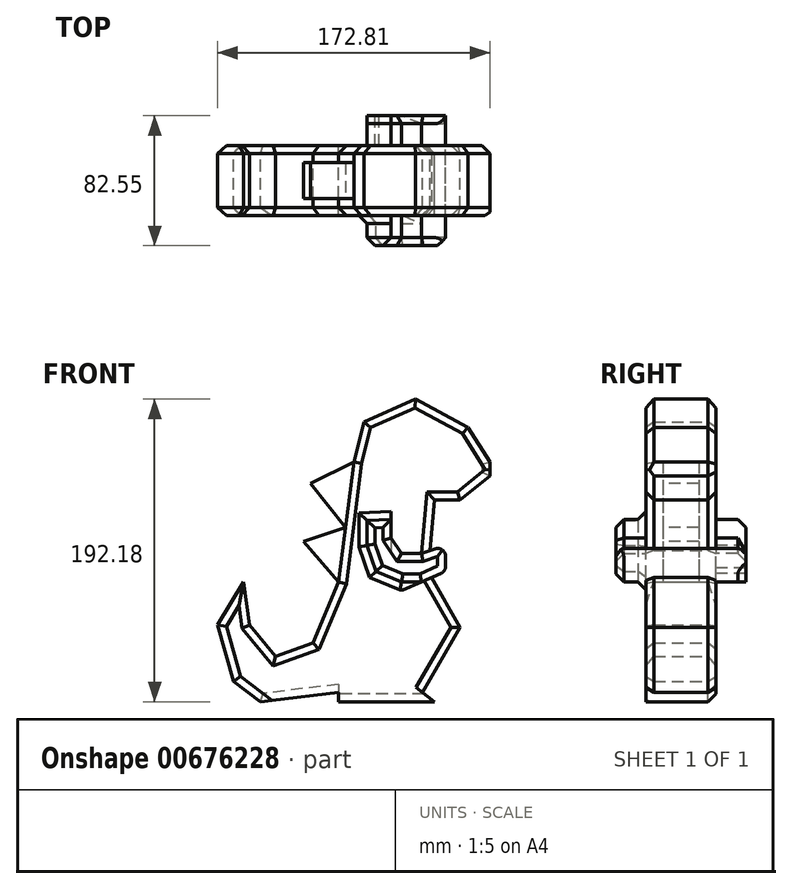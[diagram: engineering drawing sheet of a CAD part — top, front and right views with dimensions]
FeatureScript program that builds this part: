
annotation { "Feature Type Name" : "Feature", "Feature Type Description" : "" }
export const myFeature = defineFeature(function(context is Context, id is Id, definition is map)
    precondition{}
    {
        {
            var Q0;
            Q0=qCreatedBy(makeId("Front.planeOp"),FACE);
            var sketch = newSketch(context, id + "F0", { "sketchPlane" : qUnion([Q0])});
            skLineSegment(sketch, "E0", {"start": v(77.08, 51.94) * mm, "end": v(77.08, 55.91) * mm});
            skLineSegment(sketch, "E1", {"start": v(-60.47, 0) * mm, "end": v(-76.86, -27.51) * mm});
            skLineSegment(sketch, "E2", {"start": v(-76.86, -27.51) * mm, "end": v(-66.68, -63.13) * mm});
            skLineSegment(sketch, "E3", {"start": v(-60.47, 0) * mm, "end": v(-56.5, -27.51) * mm});
            skLineSegment(sketch, "E4", {"start": v(-56.5, -27.51) * mm, "end": v(-40.11, -47.38) * mm});
            skLineSegment(sketch, "E5", {"start": v(-40.11, -47.38) * mm, "end": v(-16.28, -38.93) * mm});
            skLineSegment(sketch, "E6", {"start": v(-16.28, -38.93) * mm, "end": v(0, 0) * mm});
            skPoint(sketch, "E7.start.orphan", {"position": v(68.14, 60.88) * mm});
            skPoint(sketch, "E8.end.orphan", {"position": v(45.3, 0) * mm});
            skPoint(sketch, "E8.start.orphan", {"position": v(68.14, 10.23) * mm});
            skPoint(sketch, "E9.end.orphan", {"position": v(38.54, 76.27) * mm});
            skLineSegment(sketch, "E10", {"start": v(0, 0) * mm, "end": v(9.55, 76.27) * mm});
            skLineSegment(sketch, "E11", {"start": v(-49.55, -76.18) * mm, "end": v(-66.68, -63.13) * mm});
            skLineSegment(sketch, "E12", {"start": v(-49.55, -76.18) * mm, "end": v(0, -70.22) * mm});
            skLineSegment(sketch, "E13", {"start": v(0, -70.22) * mm, "end": v(0, -76.18) * mm});
            skLineSegment(sketch, "E14", {"start": v(0, -76.18) * mm, "end": v(60.7, -76.18) * mm});
            skLineSegment(sketch, "E15", {"start": v(60.7, -76.18) * mm, "end": v(53.24, -70.22) * mm});
            skLineSegment(sketch, "E16", {"start": v(53.24, -70.22) * mm, "end": v(77.08, -29) * mm});
            skLineSegment(sketch, "E17", {"start": v(77.08, -29) * mm, "end": v(56.72, 6.75) * mm});
            skLineSegment(sketch, "E18", {"start": v(56.72, 6.75) * mm, "end": v(60.7, 51.94) * mm});
            skLineSegment(sketch, "E19", {"start": v(60.7, 51.94) * mm, "end": v(77.08, 51.94) * mm});
            skPoint(sketch, "E19.endSnap0", {"position": v(77.08, 55.91) * mm});
            skLineSegment(sketch, "E20", {"start": v(77.08, 51.94) * mm, "end": v(95.95, 67.33) * mm});
            skLineSegment(sketch, "E21", {"start": v(95.95, 67.33) * mm, "end": v(95.95, 76.27) * mm});
            skLineSegment(sketch, "E22", {"start": v(95.95, 76.27) * mm, "end": v(82.05, 98.12) * mm});
            skLineSegment(sketch, "E23", {"start": v(82.05, 98.12) * mm, "end": v(48.78, 116) * mm});
            skLineSegment(sketch, "E24", {"start": v(48.78, 116) * mm, "end": v(16, 101.6) * mm});
            skLineSegment(sketch, "E25", {"start": v(16, 101.6) * mm, "end": v(9.55, 76.27) * mm});
            skPoint(sketch, "E26.orphan", {"position": v(77.08, 76.27) * mm});
            skPoint(sketch, "E27.orphan", {"position": v(77.08, 35.55) * mm});
            skPoint(sketch, "E28.end.orphan", {"position": v(0, 76.27) * mm});
            skSolve(sketch);
        }
        {
            var Q0;
            Q0=makeQuery(id+"F0.imprint","IMPRINT",FACE,{"disambiguationData":[TD([[makeQuery(id+"F0.imprint","IMPRINT",EDGE,{"derivedFrom":sQuery(id+"F0.wireOp",EDGE,"E1")}),1.0]])]});
            extrude(context, id + "F1", {"entities" : qUnion([Q0]), "depth" : 44.45 * mm, "offsetDistance" : 25.4 * mm});
        }
        {
            var Q0;
            Q0=makeQuery(id+"F1.opExtrude","CAP_EDGE",EDGE,{"disambiguationData":[OSD([sQuery(id+"F0.wireOp",EDGE,"E24")])],"isStart":false});
            var Q1;
            Q1=makeQuery(id+"F1.opExtrude","CAP_EDGE",EDGE,{"disambiguationData":[OSD([sQuery(id+"F0.wireOp",EDGE,"E23")])],"isStart":false});
            var Q2;
            Q2=makeQuery(id+"F1.opExtrude","CAP_EDGE",EDGE,{"disambiguationData":[OSD([sQuery(id+"F0.wireOp",EDGE,"E22")])],"isStart":false});
            var Q3;
            Q3=makeQuery(id+"F1.opExtrude","CAP_EDGE",EDGE,{"disambiguationData":[OSD([sQuery(id+"F0.wireOp",EDGE,"E20")])],"isStart":false});
            var Q4;
            Q4=makeQuery(id+"F1.opExtrude","CAP_EDGE",EDGE,{"disambiguationData":[OSD([sQuery(id+"F0.wireOp",EDGE,"E19")])],"isStart":false});
            var Q5;
            Q5=makeQuery(id+"F1.opExtrude","CAP_EDGE",EDGE,{"disambiguationData":[OSD([sQuery(id+"F0.wireOp",EDGE,"E18")])],"isStart":false});
            var Q6;
            Q6=makeQuery(id+"F1.opExtrude","CAP_EDGE",EDGE,{"disambiguationData":[OSD([sQuery(id+"F0.wireOp",EDGE,"E17")])],"isStart":false});
            var Q7;
            Q7=makeQuery(id+"F1.opExtrude","CAP_EDGE",EDGE,{"disambiguationData":[OSD([sQuery(id+"F0.wireOp",EDGE,"E16")])],"isStart":false});
            var Q8;
            Q8=makeQuery(id+"F1.opExtrude","CAP_EDGE",EDGE,{"disambiguationData":[OSD([sQuery(id+"F0.wireOp",EDGE,"E10")])],"isStart":false});
            var Q9;
            Q9=makeQuery(id+"F1.opExtrude","CAP_EDGE",EDGE,{"disambiguationData":[OSD([sQuery(id+"F0.wireOp",EDGE,"E6")])],"isStart":false});
            var Q10;
            Q10=makeQuery(id+"F1.opExtrude","CAP_EDGE",EDGE,{"disambiguationData":[OSD([sQuery(id+"F0.wireOp",EDGE,"E25")])],"isStart":false});
            var Q11;
            Q11=makeQuery(id+"F1.opExtrude","CAP_EDGE",EDGE,{"disambiguationData":[OSD([sQuery(id+"F0.wireOp",EDGE,"E5")])],"isStart":false});
            var Q12;
            Q12=makeQuery(id+"F1.opExtrude","CAP_EDGE",EDGE,{"disambiguationData":[OSD([sQuery(id+"F0.wireOp",EDGE,"E4")])],"isStart":false});
            var Q13;
            Q13=makeQuery(id+"F1.opExtrude","CAP_EDGE",EDGE,{"disambiguationData":[OSD([sQuery(id+"F0.wireOp",EDGE,"E3")])],"isStart":false});
            var Q14;
            Q14=makeQuery(id+"F1.opExtrude","CAP_EDGE",EDGE,{"disambiguationData":[OSD([sQuery(id+"F0.wireOp",EDGE,"E1")])],"isStart":false});
            var Q15;
            Q15=makeQuery(id+"F1.opExtrude","CAP_EDGE",EDGE,{"disambiguationData":[OSD([sQuery(id+"F0.wireOp",EDGE,"E2")])],"isStart":false});
            var Q16;
            Q16=makeQuery(id+"F1.opExtrude","CAP_EDGE",EDGE,{"disambiguationData":[OSD([sQuery(id+"F0.wireOp",EDGE,"E11")])],"isStart":false});
            var Q17;
            Q17=makeQuery(id+"F1.opExtrude","CAP_EDGE",EDGE,{"disambiguationData":[OSD([sQuery(id+"F0.wireOp",EDGE,"E24")])],"isStart":true});
            var Q18;
            Q18=makeQuery(id+"F1.opExtrude","CAP_EDGE",EDGE,{"disambiguationData":[OSD([sQuery(id+"F0.wireOp",EDGE,"E23")])],"isStart":true});
            var Q19;
            Q19=makeQuery(id+"F1.opExtrude","CAP_EDGE",EDGE,{"disambiguationData":[OSD([sQuery(id+"F0.wireOp",EDGE,"E22")])],"isStart":true});
            var Q20;
            Q20=makeQuery(id+"F1.opExtrude","CAP_EDGE",EDGE,{"disambiguationData":[OSD([sQuery(id+"F0.wireOp",EDGE,"E21")])],"isStart":true});
            var Q21;
            Q21=makeQuery(id+"F1.opExtrude","CAP_EDGE",EDGE,{"disambiguationData":[OSD([sQuery(id+"F0.wireOp",EDGE,"E20")])],"isStart":true});
            var Q22;
            Q22=makeQuery(id+"F1.opExtrude","CAP_EDGE",EDGE,{"disambiguationData":[OSD([sQuery(id+"F0.wireOp",EDGE,"E19")])],"isStart":true});
            var Q23;
            Q23=makeQuery(id+"F1.opExtrude","CAP_EDGE",EDGE,{"disambiguationData":[OSD([sQuery(id+"F0.wireOp",EDGE,"E18")])],"isStart":true});
            var Q24;
            Q24=makeQuery(id+"F1.opExtrude","CAP_EDGE",EDGE,{"disambiguationData":[OSD([sQuery(id+"F0.wireOp",EDGE,"E17")])],"isStart":true});
            var Q25;
            Q25=makeQuery(id+"F1.opExtrude","CAP_EDGE",EDGE,{"disambiguationData":[OSD([sQuery(id+"F0.wireOp",EDGE,"E16")])],"isStart":true});
            var Q26;
            Q26=makeQuery(id+"F1.opExtrude","CAP_EDGE",EDGE,{"disambiguationData":[OSD([sQuery(id+"F0.wireOp",EDGE,"E14")])],"isStart":true});
            var Q27;
            Q27=makeQuery(id+"F1.opExtrude","CAP_EDGE",EDGE,{"disambiguationData":[OSD([sQuery(id+"F0.wireOp",EDGE,"E25")])],"isStart":true});
            var Q28;
            Q28=makeQuery(id+"F1.opExtrude","CAP_EDGE",EDGE,{"disambiguationData":[OSD([sQuery(id+"F0.wireOp",EDGE,"E10")])],"isStart":true});
            var Q29;
            Q29=makeQuery(id+"F1.opExtrude","CAP_EDGE",EDGE,{"disambiguationData":[OSD([sQuery(id+"F0.wireOp",EDGE,"E6")])],"isStart":true});
            var Q30;
            Q30=makeQuery(id+"F1.opExtrude","CAP_EDGE",EDGE,{"disambiguationData":[OSD([sQuery(id+"F0.wireOp",EDGE,"E5")])],"isStart":true});
            var Q31;
            Q31=makeQuery(id+"F1.opExtrude","CAP_EDGE",EDGE,{"disambiguationData":[OSD([sQuery(id+"F0.wireOp",EDGE,"E4")])],"isStart":true});
            var Q32;
            Q32=makeQuery(id+"F1.opExtrude","CAP_EDGE",EDGE,{"disambiguationData":[OSD([sQuery(id+"F0.wireOp",EDGE,"E3")])],"isStart":true});
            var Q33;
            Q33=makeQuery(id+"F1.opExtrude","CAP_EDGE",EDGE,{"disambiguationData":[OSD([sQuery(id+"F0.wireOp",EDGE,"E1")])],"isStart":true});
            var Q34;
            Q34=makeQuery(id+"F1.opExtrude","CAP_EDGE",EDGE,{"disambiguationData":[OSD([sQuery(id+"F0.wireOp",EDGE,"E2")])],"isStart":true});
            var Q35;
            Q35=makeQuery(id+"F1.opExtrude","CAP_EDGE",EDGE,{"disambiguationData":[OSD([sQuery(id+"F0.wireOp",EDGE,"E11")])],"isStart":true});
            var Q36;
            Q36=makeQuery(id+"F1.opExtrude","CAP_EDGE",EDGE,{"disambiguationData":[OSD([sQuery(id+"F0.wireOp",EDGE,"E12")])],"isStart":true});
            chamfer(context, id + "F2", {"entities" : qUnion([Q0, Q1, Q2, Q3, Q4, Q5, Q6, Q7, Q8, Q9, Q10, Q11, Q12, Q13, Q14, Q15, Q16, Q17, Q18, Q19, Q20, Q21, Q22, Q23, Q24, Q25, Q26, Q27, Q28, Q29, Q30, Q31, Q32, Q33, Q34, Q35, Q36]), "width" : 5.08 * mm, "tangentPropagation" : true});
        }
        {
            var Q0;
            Q0=makeQuery(id+"F1.opExtrude","CAP_FACE",FACE,{"disambiguationData":[OSD([sQuery(id+"F0.wireOp",EDGE,"E1"),sQuery(id+"F0.wireOp",EDGE,"E2"),sQuery(id+"F0.wireOp",EDGE,"E3"),sQuery(id+"F0.wireOp",EDGE,"E4"),sQuery(id+"F0.wireOp",EDGE,"E5"),sQuery(id+"F0.wireOp",EDGE,"E6"),sQuery(id+"F0.wireOp",EDGE,"E10"),sQuery(id+"F0.wireOp",EDGE,"E11"),sQuery(id+"F0.wireOp",EDGE,"E12"),sQuery(id+"F0.wireOp",EDGE,"E13"),sQuery(id+"F0.wireOp",EDGE,"E14"),sQuery(id+"F0.wireOp",EDGE,"E15"),sQuery(id+"F0.wireOp",EDGE,"E16"),sQuery(id+"F0.wireOp",EDGE,"E17"),sQuery(id+"F0.wireOp",EDGE,"E18"),sQuery(id+"F0.wireOp",EDGE,"E19"),sQuery(id+"F0.wireOp",EDGE,"E20"),sQuery(id+"F0.wireOp",EDGE,"E21"),sQuery(id+"F0.wireOp",EDGE,"E22"),sQuery(id+"F0.wireOp",EDGE,"E23"),sQuery(id+"F0.wireOp",EDGE,"E24"),sQuery(id+"F0.wireOp",EDGE,"E25")])],"isStart":true});
            var sketch = newSketch(context, id + "F3", { "sketchPlane" : qUnion([Q0])});
            skLineSegment(sketch, "E29", {"start": v(-33.23, 39.73) * mm, "end": v(-33.23, 27.8) * mm});
            skLineSegment(sketch, "E30", {"start": v(-33.23, 27.8) * mm, "end": v(-39.78, 18.16) * mm});
            skLineSegment(sketch, "E31", {"start": v(-39.78, 18.16) * mm, "end": v(-52.62, 18.16) * mm});
            skLineSegment(sketch, "E32", {"start": v(-52.62, 18.16) * mm, "end": v(-67.9, 23.17) * mm});
            skLineSegment(sketch, "E33", {"start": v(-67.9, 23.17) * mm, "end": v(-67.9, 6.61) * mm});
            skLineSegment(sketch, "E34", {"start": v(-67.9, 6.61) * mm, "end": v(-52.62, 0) * mm});
            skLineSegment(sketch, "E35", {"start": v(-52.62, 0) * mm, "end": v(-39.78, 0) * mm});
            skLineSegment(sketch, "E36", {"start": v(-39.78, 0) * mm, "end": v(-23.6, 6.61) * mm});
            skLineSegment(sketch, "E37", {"start": v(-23.6, 6.61) * mm, "end": v(-17.83, 23.17) * mm});
            skLineSegment(sketch, "E38", {"start": v(-17.83, 23.17) * mm, "end": v(-17.83, 38.96) * mm});
            skLineSegment(sketch, "E39", {"start": v(-17.83, 38.96) * mm, "end": v(-33.23, 39.73) * mm});
            skSolve(sketch);
        }
        {
            var Q0;
            {var subQ9=sQuery(id+"F3.wireOp",EDGE,"E32");Q0=makeQuery(id+"F3.imprint","IMPRINT",FACE,{"disambiguationData":[TD([[makeQuery(id+"F3.imprint","IMPRINT",EDGE,{"derivedFrom":subQ9}),1.0]])]});}
            var Q1;
            Q1=makeQuery(id+"F3.imprint","IMPRINT",FACE,{"disambiguationData":[TD([[makeQuery(id+"F3.imprint","IMPRINT",EDGE,{"derivedFrom":sQuery(id+"F3.wireOp",EDGE,"E29")}),1.0]])]});
            extrude(context, id + "F4", {"entities" : qUnion([Q0, Q1]), "operationType" : NewBodyOperationType.ADD, "oppositeDirection" : true, "depth" : 63.5 * mm, "offsetDistance" : 25.4 * mm});
        }
        {
            var Q0;
            Q0=qSketchRegion(id+"F3",true);
            extrude(context, id + "F5", {"entities" : qUnion([Q0]), "operationType" : NewBodyOperationType.ADD, "depth" : 19.05 * mm, "offsetDistance" : 25.4 * mm});
        }
        {
            var Q0;
            Q0=makeQuery(id+"F5.opExtrude","CAP_EDGE",EDGE,{"disambiguationData":[OSD([sQuery(id+"F3.wireOp",EDGE,"E39")])],"isStart":true});
            var Q1;
            Q1=makeQuery(id+"F5.opExtrude","CAP_EDGE",EDGE,{"disambiguationData":[OSD([sQuery(id+"F3.wireOp",EDGE,"E39")])],"isStart":false});
            var Q2;
            Q2=makeQuery(id+"F5.opExtrude","CAP_EDGE",EDGE,{"disambiguationData":[OSD([sQuery(id+"F3.wireOp",EDGE,"E32")])],"isStart":false});
            var Q3;
            Q3=makeQuery(id+"F5.opExtrude","CAP_EDGE",EDGE,{"disambiguationData":[OSD([sQuery(id+"F3.wireOp",EDGE,"E31")])],"isStart":false});
            var Q4;
            Q4=makeQuery(id+"F5.opExtrude","CAP_EDGE",EDGE,{"disambiguationData":[OSD([sQuery(id+"F3.wireOp",EDGE,"E30")])],"isStart":false});
            var Q5;
            Q5=makeQuery(id+"F5.opExtrude","CAP_EDGE",EDGE,{"disambiguationData":[OSD([sQuery(id+"F3.wireOp",EDGE,"E38")])],"isStart":true});
            var Q6;
            Q6=makeQuery(id+"F5.opExtrude","CAP_EDGE",EDGE,{"disambiguationData":[OSD([sQuery(id+"F3.wireOp",EDGE,"E37")])],"isStart":true});
            var Q7;
            Q7=makeQuery(id+"F5.opExtrude","SWEPT_EDGE",EDGE,{"disambiguationData":[OSD([sQuery(id+"F3.wireOp",EDGE,"E36"),sQuery(id+"F3.wireOp",EDGE,"E37")])]});
            var Q8;
            Q8=makeQuery(id+"F5.opExtrude","CAP_EDGE",EDGE,{"disambiguationData":[OSD([sQuery(id+"F3.wireOp",EDGE,"E35")])],"isStart":true});
            var Q9;
            Q9=makeQuery(id+"F5.opExtrude","CAP_EDGE",EDGE,{"disambiguationData":[OSD([sQuery(id+"F3.wireOp",EDGE,"E34")])],"isStart":false});
            var Q10;
            Q10=makeQuery(id+"F4.boolean.opBoolean","INTERSECT",EDGE,{"derivedFrom":[makeQuery(id+"F1.opExtrude","CAP_FACE",FACE,{"disambiguationData":[OSD([sQuery(id+"F0.wireOp",EDGE,"E1"),sQuery(id+"F0.wireOp",EDGE,"E2"),sQuery(id+"F0.wireOp",EDGE,"E3"),sQuery(id+"F0.wireOp",EDGE,"E4"),sQuery(id+"F0.wireOp",EDGE,"E5"),sQuery(id+"F0.wireOp",EDGE,"E6"),sQuery(id+"F0.wireOp",EDGE,"E10"),sQuery(id+"F0.wireOp",EDGE,"E11"),sQuery(id+"F0.wireOp",EDGE,"E12"),sQuery(id+"F0.wireOp",EDGE,"E13"),sQuery(id+"F0.wireOp",EDGE,"E14"),sQuery(id+"F0.wireOp",EDGE,"E15"),sQuery(id+"F0.wireOp",EDGE,"E16"),sQuery(id+"F0.wireOp",EDGE,"E17"),sQuery(id+"F0.wireOp",EDGE,"E18"),sQuery(id+"F0.wireOp",EDGE,"E19"),sQuery(id+"F0.wireOp",EDGE,"E20"),sQuery(id+"F0.wireOp",EDGE,"E21"),sQuery(id+"F0.wireOp",EDGE,"E22"),sQuery(id+"F0.wireOp",EDGE,"E23"),sQuery(id+"F0.wireOp",EDGE,"E24"),sQuery(id+"F0.wireOp",EDGE,"E25")])],"isStart":false}),makeQuery(id+"F4.opExtrude","SWEPT_FACE",FACE,{"disambiguationData":[OSD([sQuery(id+"F3.wireOp",EDGE,"E39")])]})]});
            var Q11;
            Q11=makeQuery(id+"F4.opExtrude","CAP_EDGE",EDGE,{"disambiguationData":[OSD([sQuery(id+"F3.wireOp",EDGE,"E39")])],"isStart":false});
            var Q12;
            Q12=makeQuery(id+"F4.opExtrude","CAP_EDGE",EDGE,{"disambiguationData":[OSD([sQuery(id+"F3.wireOp",EDGE,"E29")])],"isStart":false});
            var Q13;
            Q13=makeQuery(id+"F4.opExtrude","CAP_EDGE",EDGE,{"disambiguationData":[OSD([sQuery(id+"F3.wireOp",EDGE,"E30")])],"isStart":false});
            var Q14;
            Q14=makeQuery(id+"F4.opExtrude","CAP_EDGE",EDGE,{"disambiguationData":[OSD([sQuery(id+"F3.wireOp",EDGE,"E31")])],"isStart":false});
            var Q15;
            Q15=makeQuery(id+"F4.opExtrude","CAP_EDGE",EDGE,{"disambiguationData":[OSD([sQuery(id+"F3.wireOp",EDGE,"E32")])],"isStart":false});
            var Q16;
            Q16=makeQuery(id+"F4.boolean.opBoolean","INTERSECT",EDGE,{"derivedFrom":[makeQuery(id+"F1.opExtrude","CAP_FACE",FACE,{"disambiguationData":[OSD([sQuery(id+"F0.wireOp",EDGE,"E1"),sQuery(id+"F0.wireOp",EDGE,"E2"),sQuery(id+"F0.wireOp",EDGE,"E3"),sQuery(id+"F0.wireOp",EDGE,"E4"),sQuery(id+"F0.wireOp",EDGE,"E5"),sQuery(id+"F0.wireOp",EDGE,"E6"),sQuery(id+"F0.wireOp",EDGE,"E10"),sQuery(id+"F0.wireOp",EDGE,"E11"),sQuery(id+"F0.wireOp",EDGE,"E12"),sQuery(id+"F0.wireOp",EDGE,"E13"),sQuery(id+"F0.wireOp",EDGE,"E14"),sQuery(id+"F0.wireOp",EDGE,"E15"),sQuery(id+"F0.wireOp",EDGE,"E16"),sQuery(id+"F0.wireOp",EDGE,"E17"),sQuery(id+"F0.wireOp",EDGE,"E18"),sQuery(id+"F0.wireOp",EDGE,"E19"),sQuery(id+"F0.wireOp",EDGE,"E20"),sQuery(id+"F0.wireOp",EDGE,"E21"),sQuery(id+"F0.wireOp",EDGE,"E22"),sQuery(id+"F0.wireOp",EDGE,"E23"),sQuery(id+"F0.wireOp",EDGE,"E24"),sQuery(id+"F0.wireOp",EDGE,"E25")])],"isStart":false}),makeQuery(id+"F4.opExtrude","SWEPT_FACE",FACE,{"disambiguationData":[OSD([sQuery(id+"F3.wireOp",EDGE,"E35")])]})]});
            var Q17;
            Q17=makeQuery(id+"F4.boolean.opBoolean","INTERSECT",EDGE,{"derivedFrom":[makeQuery(id+"F1.opExtrude","CAP_FACE",FACE,{"disambiguationData":[OSD([sQuery(id+"F0.wireOp",EDGE,"E1"),sQuery(id+"F0.wireOp",EDGE,"E2"),sQuery(id+"F0.wireOp",EDGE,"E3"),sQuery(id+"F0.wireOp",EDGE,"E4"),sQuery(id+"F0.wireOp",EDGE,"E5"),sQuery(id+"F0.wireOp",EDGE,"E6"),sQuery(id+"F0.wireOp",EDGE,"E10"),sQuery(id+"F0.wireOp",EDGE,"E11"),sQuery(id+"F0.wireOp",EDGE,"E12"),sQuery(id+"F0.wireOp",EDGE,"E13"),sQuery(id+"F0.wireOp",EDGE,"E14"),sQuery(id+"F0.wireOp",EDGE,"E15"),sQuery(id+"F0.wireOp",EDGE,"E16"),sQuery(id+"F0.wireOp",EDGE,"E17"),sQuery(id+"F0.wireOp",EDGE,"E18"),sQuery(id+"F0.wireOp",EDGE,"E19"),sQuery(id+"F0.wireOp",EDGE,"E20"),sQuery(id+"F0.wireOp",EDGE,"E21"),sQuery(id+"F0.wireOp",EDGE,"E22"),sQuery(id+"F0.wireOp",EDGE,"E23"),sQuery(id+"F0.wireOp",EDGE,"E24"),sQuery(id+"F0.wireOp",EDGE,"E25")])],"isStart":false}),makeQuery(id+"F4.opExtrude","SWEPT_FACE",FACE,{"disambiguationData":[OSD([sQuery(id+"F3.wireOp",EDGE,"E36")])]})]});
            var Q18;
            Q18=makeQuery(id+"F4.boolean.opBoolean","INTERSECT",EDGE,{"derivedFrom":[makeQuery(id+"F1.opExtrude","CAP_FACE",FACE,{"disambiguationData":[OSD([sQuery(id+"F0.wireOp",EDGE,"E1"),sQuery(id+"F0.wireOp",EDGE,"E2"),sQuery(id+"F0.wireOp",EDGE,"E3"),sQuery(id+"F0.wireOp",EDGE,"E4"),sQuery(id+"F0.wireOp",EDGE,"E5"),sQuery(id+"F0.wireOp",EDGE,"E6"),sQuery(id+"F0.wireOp",EDGE,"E10"),sQuery(id+"F0.wireOp",EDGE,"E11"),sQuery(id+"F0.wireOp",EDGE,"E12"),sQuery(id+"F0.wireOp",EDGE,"E13"),sQuery(id+"F0.wireOp",EDGE,"E14"),sQuery(id+"F0.wireOp",EDGE,"E15"),sQuery(id+"F0.wireOp",EDGE,"E16"),sQuery(id+"F0.wireOp",EDGE,"E17"),sQuery(id+"F0.wireOp",EDGE,"E18"),sQuery(id+"F0.wireOp",EDGE,"E19"),sQuery(id+"F0.wireOp",EDGE,"E20"),sQuery(id+"F0.wireOp",EDGE,"E21"),sQuery(id+"F0.wireOp",EDGE,"E22"),sQuery(id+"F0.wireOp",EDGE,"E23"),sQuery(id+"F0.wireOp",EDGE,"E24"),sQuery(id+"F0.wireOp",EDGE,"E25")])],"isStart":false}),makeQuery(id+"F4.opExtrude","SWEPT_FACE",FACE,{"disambiguationData":[OSD([sQuery(id+"F3.wireOp",EDGE,"E38")])]})]});
            var Q19;
            Q19=makeQuery(id+"F4.boolean.opBoolean","INTERSECT",EDGE,{"derivedFrom":[makeQuery(id+"F1.opExtrude","CAP_FACE",FACE,{"disambiguationData":[OSD([sQuery(id+"F0.wireOp",EDGE,"E1"),sQuery(id+"F0.wireOp",EDGE,"E2"),sQuery(id+"F0.wireOp",EDGE,"E3"),sQuery(id+"F0.wireOp",EDGE,"E4"),sQuery(id+"F0.wireOp",EDGE,"E5"),sQuery(id+"F0.wireOp",EDGE,"E6"),sQuery(id+"F0.wireOp",EDGE,"E10"),sQuery(id+"F0.wireOp",EDGE,"E11"),sQuery(id+"F0.wireOp",EDGE,"E12"),sQuery(id+"F0.wireOp",EDGE,"E13"),sQuery(id+"F0.wireOp",EDGE,"E14"),sQuery(id+"F0.wireOp",EDGE,"E15"),sQuery(id+"F0.wireOp",EDGE,"E16"),sQuery(id+"F0.wireOp",EDGE,"E17"),sQuery(id+"F0.wireOp",EDGE,"E18"),sQuery(id+"F0.wireOp",EDGE,"E19"),sQuery(id+"F0.wireOp",EDGE,"E20"),sQuery(id+"F0.wireOp",EDGE,"E21"),sQuery(id+"F0.wireOp",EDGE,"E22"),sQuery(id+"F0.wireOp",EDGE,"E23"),sQuery(id+"F0.wireOp",EDGE,"E24"),sQuery(id+"F0.wireOp",EDGE,"E25")])],"isStart":false}),makeQuery(id+"F4.opExtrude","SWEPT_FACE",FACE,{"disambiguationData":[OSD([sQuery(id+"F3.wireOp",EDGE,"E37")])]})]});
            chamfer(context, id + "F6", {"entities" : qUnion([Q0, Q1, Q2, Q3, Q4, Q5, Q6, Q7, Q8, Q9, Q10, Q11, Q12, Q13, Q14, Q15, Q16, Q17, Q18, Q19]), "width" : 5.08 * mm, "tangentPropagation" : true});
        }
        {
            var Q0;
            Q0=makeQuery(id+"F1.opExtrude","SWEPT_FACE",FACE,{"disambiguationData":[OSD([sQuery(id+"F0.wireOp",EDGE,"E10")])]});
            var sketch = newSketch(context, id + "F7", { "sketchPlane" : qUnion([Q0])});
            skLineSegment(sketch, "E40.bottom", {"start": v(17.14, 76.86) * mm, "end": v(26.38, 76.86) * mm});
            skLineSegment(sketch, "E40.top", {"start": v(17.14, 0) * mm, "end": v(26.38, 0) * mm});
            skLineSegment(sketch, "E40.left", {"start": v(17.14, 76.86) * mm, "end": v(17.14, 0) * mm});
            skLineSegment(sketch, "E40.right", {"start": v(26.38, 76.86) * mm, "end": v(26.38, 0) * mm});
            skSolve(sketch);
        }
        {
            var Q0;
            Q0=qSketchRegion(id+"F7",true);
            extrude(context, id + "F8", {"entities" : qUnion([Q0]), "operationType" : NewBodyOperationType.ADD, "depth" : 25.4 * mm, "offsetDistance" : 25.4 * mm});
        }
        {
            var Q0;
            Q0=makeQuery(id+"F8.opExtrude","SWEPT_FACE",FACE,{"disambiguationData":[OSD([sQuery(id+"F7.wireOp",EDGE,"E40.left")])]});
            var sketch = newSketch(context, id + "F9", { "sketchPlane" : qUnion([Q0])});
            skLineSegment(sketch, "E41", {"start": v(-9.55, 76.27) * mm, "end": v(17.76, 62.62) * mm});
            skLineSegment(sketch, "E42", {"start": v(17.76, 62.62) * mm, "end": v(-4.33, 34.58) * mm});
            skLineSegment(sketch, "E43", {"start": v(-4.33, 34.58) * mm, "end": v(22.4, 25.6) * mm});
            skLineSegment(sketch, "E44", {"start": v(22.4, 25.6) * mm, "end": v(0, 0) * mm});
            skSolve(sketch);
        }
        {
            var Q0;
            {var subQ0=sQuery(id+"F9.wireOp",EDGE,"E41");Q0=makeQuery(id+"F9.imprint","IMPRINT",FACE,{"disambiguationData":[TD([[makeQuery(id+"F9.imprint","IMPRINT",EDGE,{"derivedFrom":subQ0}),-1.0]])]});}
            var Q1;
            {var subQ0=sQuery(id+"F9.wireOp",EDGE,"E43");Q1=makeQuery(id+"F9.imprint","IMPRINT",FACE,{"disambiguationData":[TD([[makeQuery(id+"F9.imprint","IMPRINT",EDGE,{"derivedFrom":subQ0}),-1.0]])]});}
            extrude(context, id + "F10", {"entities" : qUnion([Q0, Q1]), "operationType" : NewBodyOperationType.ADD, "depth" : 6.35 * mm, "offsetDistance" : 25.4 * mm});
        }
        {
            var Q0;
            Q0=makeQuery(id+"F10.opExtrude","CAP_FACE",FACE,{"disambiguationData":[OSD([sQuery(id+"F7.wireOp",EDGE,"E40.left"),sQuery(id+"F9.wireOp",EDGE,"E41"),sQuery(id+"F9.wireOp",EDGE,"E42")])],"isStart":false});
            var Q1;
            Q1=makeQuery(id+"F10.opExtrude","CAP_FACE",FACE,{"disambiguationData":[OSD([sQuery(id+"F7.wireOp",EDGE,"E40.left"),sQuery(id+"F9.wireOp",EDGE,"E43"),sQuery(id+"F9.wireOp",EDGE,"E44")])],"isStart":false});
            extrude(context, id + "F11", {"entities" : qUnion([Q0, Q1]), "operationType" : NewBodyOperationType.ADD, "oppositeDirection" : true, "depth" : 22.6 * mm, "offsetDistance" : 25.4 * mm});
        }
        {
            var Q0;
            {var subQ0=sQuery(id+"F3.wireOp",EDGE,"E33");var subQ1=sQuery(id+"F3.wireOp",EDGE,"E32");Q0=makeQuery(id+"F5.boolean.opBoolean","MERGE",EDGE,{"derivedFrom":[makeQuery(id+"F4.opExtrude","SWEPT_EDGE",EDGE,{"disambiguationData":[OSD([subQ1,subQ0])]}),makeQuery(id+"F5.opExtrude","SWEPT_EDGE",EDGE,{"disambiguationData":[OSD([subQ1,subQ0])]})]});}
            var Q1;
            {var subQ0=sQuery(id+"F3.wireOp",EDGE,"E34");var subQ1=sQuery(id+"F3.wireOp",EDGE,"E33");Q1=makeQuery(id+"F5.boolean.opBoolean","MERGE",EDGE,{"derivedFrom":[makeQuery(id+"F4.opExtrude","SWEPT_EDGE",EDGE,{"disambiguationData":[OSD([subQ1,subQ0])]}),makeQuery(id+"F5.opExtrude","SWEPT_EDGE",EDGE,{"disambiguationData":[OSD([subQ1,subQ0])]})]});}
            fillet(context, id + "F12", {"entities" : qUnion([Q0, Q1]), "radius" : 5.08 * mm, "tangentPropagation" : true, "allowEdgeOverflow" : false});
        }
        {
            var Q0;
            Q0=makeQuery(id+"F4.opExtrude","CAP_EDGE",EDGE,{"disambiguationData":[OSD([sQuery(id+"F3.wireOp",EDGE,"E34")])],"isStart":false});
            var Q1;
            Q1=makeQuery(id+"F4.opExtrude","CAP_EDGE",EDGE,{"disambiguationData":[OSD([sQuery(id+"F3.wireOp",EDGE,"E36")])],"isStart":false});
            var Q2;
            Q2=makeQuery(id+"F4.opExtrude","CAP_EDGE",EDGE,{"disambiguationData":[OSD([sQuery(id+"F3.wireOp",EDGE,"E37")])],"isStart":false});
            var Q3;
            Q3=makeQuery(id+"F4.opExtrude","CAP_EDGE",EDGE,{"disambiguationData":[OSD([sQuery(id+"F3.wireOp",EDGE,"E38")])],"isStart":false});
            var Q4;
            Q4=makeQuery(id+"F4.opExtrude","CAP_EDGE",EDGE,{"disambiguationData":[OSD([sQuery(id+"F3.wireOp",EDGE,"E35")])],"isStart":false});
            chamfer(context, id + "F13", {"entities" : qUnion([Q0, Q1, Q2, Q3, Q4]), "width" : 5.08 * mm, "tangentPropagation" : true});
        }
        {
            var Q0;
            {var subQ0=sQuery(id+"F7.wireOp",EDGE,"E40.right");var subQ1=makeQuery(id+"F8.opExtrude","SWEPT_FACE",FACE,{"disambiguationData":[OSD([subQ0])]});var subQ2=sQuery(id+"F7.wireOp",EDGE,"E40.bottom");Q0=makeQuery(id+"F11.boolean.opBoolean","SPLIT",FACE,{"disambiguationData":[TD([makeQuery(id+"F1.opExtrude","SWEPT_FACE",FACE,{"disambiguationData":[OSD([sQuery(id+"F0.wireOp",EDGE,"E25")])]}),makeQuery(id+"F8.opExtrude","SWEPT_FACE",FACE,{"disambiguationData":[OSD([subQ2])]}),makeQuery(id+"F8.opExtrude","CAP_FACE",FACE,{"disambiguationData":[OSD([subQ2,sQuery(id+"F7.wireOp",EDGE,"E40.top"),sQuery(id+"F7.wireOp",EDGE,"E40.left"),subQ0])],"isStart":false}),subQ1,makeQuery(id+"F11.opExtrude","SWEPT_FACE",FACE,{"disambiguationData":[OSD([sQuery(id+"F9.wireOp",EDGE,"E41")])]}),makeQuery(id+"F11.opExtrude","SWEPT_FACE",FACE,{"disambiguationData":[OSD([sQuery(id+"F9.wireOp",EDGE,"E42")])]})])],"derivedFrom":subQ1});}
            var Q1;
            {var subQ0=sQuery(id+"F7.wireOp",EDGE,"E40.right");var subQ1=makeQuery(id+"F8.opExtrude","SWEPT_FACE",FACE,{"disambiguationData":[OSD([subQ0])]});Q1=makeQuery(id+"F11.boolean.opBoolean","SPLIT",FACE,{"disambiguationData":[TD([makeQuery(id+"F8.opExtrude","CAP_FACE",FACE,{"disambiguationData":[OSD([sQuery(id+"F7.wireOp",EDGE,"E40.bottom"),sQuery(id+"F7.wireOp",EDGE,"E40.top"),sQuery(id+"F7.wireOp",EDGE,"E40.left"),subQ0])],"isStart":false}),subQ1,makeQuery(id+"F11.opExtrude","SWEPT_FACE",FACE,{"disambiguationData":[OSD([sQuery(id+"F9.wireOp",EDGE,"E41")])]}),makeQuery(id+"F11.opExtrude","SWEPT_FACE",FACE,{"disambiguationData":[OSD([sQuery(id+"F9.wireOp",EDGE,"E42")])]}),makeQuery(id+"F11.opExtrude","SWEPT_FACE",FACE,{"disambiguationData":[OSD([sQuery(id+"F9.wireOp",EDGE,"E43")])]}),makeQuery(id+"F11.opExtrude","SWEPT_FACE",FACE,{"disambiguationData":[OSD([sQuery(id+"F9.wireOp",EDGE,"E44")])]})])],"derivedFrom":subQ1});}
            var Q2;
            {var subQ0=sQuery(id+"F7.wireOp",EDGE,"E40.right");var subQ1=makeQuery(id+"F8.opExtrude","SWEPT_FACE",FACE,{"disambiguationData":[OSD([subQ0])]});var subQ2=sQuery(id+"F7.wireOp",EDGE,"E40.top");Q2=makeQuery(id+"F11.boolean.opBoolean","SPLIT",FACE,{"disambiguationData":[TD([makeQuery(id+"F1.opExtrude","SWEPT_FACE",FACE,{"disambiguationData":[OSD([sQuery(id+"F0.wireOp",EDGE,"E6")])]}),makeQuery(id+"F8.opExtrude","CAP_FACE",FACE,{"disambiguationData":[OSD([sQuery(id+"F7.wireOp",EDGE,"E40.bottom"),subQ2,sQuery(id+"F7.wireOp",EDGE,"E40.left"),subQ0])],"isStart":false}),makeQuery(id+"F8.opExtrude","SWEPT_FACE",FACE,{"disambiguationData":[OSD([subQ2])]}),subQ1,makeQuery(id+"F11.opExtrude","SWEPT_FACE",FACE,{"disambiguationData":[OSD([sQuery(id+"F9.wireOp",EDGE,"E43")])]}),makeQuery(id+"F11.opExtrude","SWEPT_FACE",FACE,{"disambiguationData":[OSD([sQuery(id+"F9.wireOp",EDGE,"E44")])]})])],"derivedFrom":subQ1});}
            extrude(context, id + "F14", {"entities" : qUnion([Q0, Q1, Q2]), "operationType" : NewBodyOperationType.REMOVE, "oppositeDirection" : true, "depth" : 50.8 * mm, "offsetDistance" : 25.4 * mm});
        }
    });
